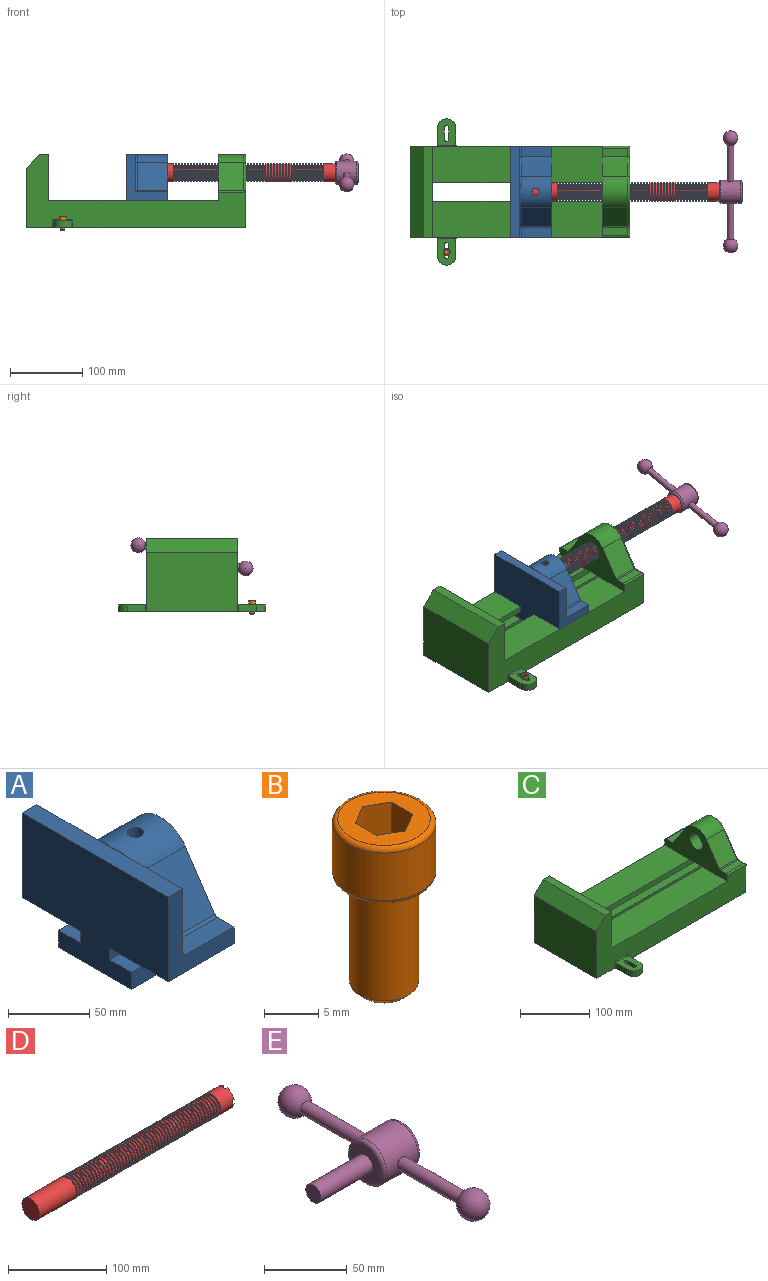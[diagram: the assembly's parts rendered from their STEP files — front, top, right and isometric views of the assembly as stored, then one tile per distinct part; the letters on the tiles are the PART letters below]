
ASSEMBLY  parts=5 mates=5
PART A: 36 faces, bbox 57.2x127x89 mm
  f0: plane 57.15x50.8mm, normal (0,0,-1), area 2903.2mm2, adj f6,f9,f10,f23
  f1: cylinder r=12.7mm len=44.45mm, axis (1,0,0), area 3464.3mm2, adj f6,f15,f16
  f2: plane 41.91x14.52mm, normal (0,0,1), area 608.5mm2, adj f6,f11,f24,f25
  f3: plane 51.86x48.26mm, normal (1,0,0), area 1495.7mm2, adj f8,f10,f31,f33,f35
  f4: plane 51.86x48.26mm, normal (1,0,0), area 1495.7mm2, adj f8,f11,f24,f28,f29
  f5: plane 57.15x50.8mm, normal (0,0,-1), area 2903.2mm2, adj f6,f9,f11,f22
  f6: plane 127x85.09mm, normal (1,0,0), area 5190.6mm2, adj f0,f1,f2,f5,f7,f10,f11,f12
  f7: plane 41.91x14.52mm, normal (0,0,1), area 608.5mm2, adj f6,f10,f30,f31
  f8: plane 127x12.7mm, normal (0,0,1), area 1612.9mm2, adj f3,f4,f9,f10,f11,f26,f34
  f9: plane 127x85.09mm, normal (-1,0,0), area 9096.8mm2, adj f0,f5,f8,f10,f11,f17,f18,f19
  f10: plane 63.5x57.15mm, normal (0,-1,0), area 1372.3mm2, adj f0,f3,f6,f7,f8,f9,f31
  f11: plane 63.5x57.15mm, normal (0,1,0), area 1372.3mm2, adj f2,f4,f5,f6,f8,f9,f24
  f12: plane 41.91x38.43mm, normal (0,-0.83,0.56), area 1939.2mm2, adj f6,f13,f30,f33
  f13: cylinder r=25.4mm len=44.45mm, axis (1,0,0), area 2026.5mm2, adj f6,f12,f14,f16,f26,f28,f34,f35
  f14: plane 41.91x38.43mm, normal (0,0.83,0.56), area 1939.2mm2, adj f6,f13,f25,f29
  f15: plane 25.4x25.4mm, normal (1,0,0), area 506.7mm2, adj f1
  f16: cylinder r=5.08mm len=13.76mm, axis (0,0,1), area 414mm2, adj f1,f13
  f17: plane 57.15x19.05mm, normal (0,0,1), area 1088.7mm2, adj f6,f9,f18,f23
  f18: plane 57.15x12.7mm, normal (0,-1,0), area 725.8mm2, adj f6,f9,f17,f19
  f19: plane 63.5x57.15mm, normal (0,0,-1), area 3629mm2, adj f6,f9,f18,f20
  f20: plane 57.15x12.7mm, normal (0,1,0), area 725.8mm2, adj f6,f9,f19,f21
  f21: plane 57.15x19.05mm, normal (0,0,1), area 1088.7mm2, adj f6,f9,f20,f22
  f22: plane 57.15x8.89mm, normal (0,1,0), area 508.1mm2, adj f5,f6,f9,f21
  f23: plane 57.15x8.89mm, normal (0,-1,0), area 508.1mm2, adj f0,f6,f9,f17
  f24: cylinder r=2.54mm len=14.52mm, axis (0,-1,0), area 57.9mm2, adj f2,f4,f11,f27
  f25: cylinder r=2.54mm len=41.91mm, axis (1,0,0), area 104.3mm2, adj f2,f6,f14,f27
  f26: bspline ~12.24x2.8mm, area 20.9mm2, adj f8,f13,f28
  f27: sphere r=2.54mm, area 6.3mm2, adj f24,f25,f29
  f28: torus R=27.94mm, axis (1,0,0), area 57.8mm2, adj f4,f13,f26,f29
  f29: cylinder r=2.54mm len=39.84mm, axis (0,-0.56,0.83), area 184.6mm2, adj f4,f14,f27,f28
  f30: cylinder r=2.54mm len=41.91mm, axis (1,0,0), area 104.3mm2, adj f6,f7,f12,f32
  f31: cylinder r=2.54mm len=14.52mm, axis (0,-1,0), area 57.9mm2, adj f3,f7,f10,f32
  f32: sphere r=2.54mm, area 6.3mm2, adj f30,f31,f33
  f33: cylinder r=2.54mm len=39.84mm, axis (0,-0.56,-0.83), area 184.6mm2, adj f3,f12,f32,f35
  f34: bspline ~12.24x2.8mm, area 20.9mm2, adj f8,f13,f35
  f35: torus R=27.94mm, axis (1,0,0), area 57.8mm2, adj f3,f13,f33,f34
PART B: 15 faces, bbox 10.3x10.3x19.1 mm
  f0: plane 8.51x8.51mm, normal (0,0,1), area 37.2mm2, adj f5,f6,f7,f8,f9,f10,f14
  f1: cylinder r=3.17mm len=11.94mm, axis (0,0,1), area 238.2mm2, adj f4,f12
  f2: plane 4.83x4.83mm, normal (0,0,-1), area 18.3mm2, adj f12
  f3: cylinder r=4.76mm len=9.53mm, axis (0,0,-1), area 159.6mm2, adj f13,f14
  f4: plane 8.51x8.51mm, normal (0,0,-1), area 25.2mm2, adj f1,f13
  f5: plane 4.83x2.38mm, normal (-0.5,-0.87,0), area 13.3mm2, adj f0,f6,f10,f11
  f6: plane 4.83x2.38mm, normal (0.5,-0.87,0), area 13.3mm2, adj f0,f5,f7,f11
  f7: plane 4.83x2.75mm, normal (1,0,0), area 13.3mm2, adj f0,f6,f8,f11
  f8: plane 4.83x2.38mm, normal (0.5,0.87,0), area 13.3mm2, adj f0,f7,f9,f11
  f9: plane 4.83x2.38mm, normal (-0.5,0.87,0), area 13.3mm2, adj f0,f8,f10,f11
  f10: plane 4.83x2.75mm, normal (-1,0,0), area 13.3mm2, adj f0,f5,f9,f11
  f11: plane 5.5x4.76mm, normal (0,0,1), area 19.6mm2, adj f5,f6,f7,f8,f9,f10
  f12: cone r=3.17mm half-angle=45deg, axis (0,0,1), area 18.9mm2, adj f1,f2
  f13: torus R=4.25mm, axis (0,0,1), area 23mm2, adj f3,f4
  f14: torus R=4.25mm, axis (0,0,1), area 23mm2, adj f0,f3
PART C: 61 faces, bbox 304.8x203.2x103.7 mm
  f0: plane 304.8x101.6mm, normal (0,1,0), area 13520.3mm2, adj f3,f4,f5,f6,f7,f8,f9,f16
  f1: plane 304.8x101.6mm, normal (0,-1,0), area 13520.3mm2, adj f2,f3,f5,f6,f7,f8,f9,f16
  f2: plane 234.95x50.8mm, normal (0,0,1), area 11935.5mm2, adj f1,f5,f16,f26
  f3: plane 127x99.06mm, normal (1,0,0), area 7097.5mm2, adj f0,f1,f9,f14,f17,f18,f19,f20
  f4: plane 234.95x50.8mm, normal (0,0,1), area 11935.5mm2, adj f0,f5,f16,f27
  f5: plane 127x101.6mm, normal (1,0,0), area 9516.1mm2, adj f0,f1,f2,f4,f6,f9,f18,f19
  f6: plane 127x12.7mm, normal (0,0,1), area 1612.9mm2, adj f0,f1,f5,f7
  f7: plane 127x19.05mm, normal (-0.71,0,0.71), area 3421.5mm2, adj f0,f1,f6,f8
  f8: plane 127x82.55mm, normal (-1,0,0), area 10483.8mm2, adj f0,f1,f7,f9
  f9: plane 304.8x203.2mm, normal (0,0,-1), area 33298.3mm2, adj f0,f1,f3,f5,f8,f21,f22,f39
  f10: plane 35.56x11.98mm, normal (0,0,1), area 426mm2, adj f16,f28,f29,f30
  f11: plane 38.43x35.56mm, normal (0,0.83,0.56), area 1645.4mm2, adj f12,f16,f29,f32
  f12: cylinder r=25.4mm len=42.19mm, axis (1,0,0), area 1770.2mm2, adj f11,f13,f16,f33
  f13: plane 38.43x35.56mm, normal (0,-0.83,0.56), area 1645.4mm2, adj f12,f16,f34,f35
  f14: cylinder r=12.7mm len=38.1mm, axis (1,0,0), area 3040.2mm2, adj f3,f16
  f15: plane 35.56x11.98mm, normal (0,0,1), area 426mm2, adj f16,f34,f36,f38
  f16: plane 127x63.5mm, normal (-1,0,0), area 4155.5mm2, adj f0,f1,f2,f4,f10,f11,f12,f13
  f17: plane 38.1x25.4mm, normal (0,0,-1), area 967.7mm2, adj f3,f16,f26,f27
  f18: plane 273.05x19.05mm, normal (0,0,-1), area 5201.6mm2, adj f3,f5,f19,f26
  f19: plane 273.05x12.7mm, normal (0,1,0), area 3467.7mm2, adj f3,f5,f18,f20
  f20: plane 273.05x19.05mm, normal (0,0,1), area 5201.6mm2, adj f3,f5,f19,f21
  f21: plane 273.05x16.51mm, normal (0,1,0), area 4508.1mm2, adj f3,f5,f9,f20
  f22: plane 273.05x16.51mm, normal (0,-1,0), area 4508.1mm2, adj f3,f5,f9,f23
  f23: plane 273.05x19.05mm, normal (0,0,1), area 5201.6mm2, adj f3,f5,f22,f24
  f24: plane 273.05x12.7mm, normal (0,-1,0), area 3467.7mm2, adj f3,f5,f23,f25
  f25: plane 273.05x19.05mm, normal (0,0,-1), area 5201.6mm2, adj f3,f5,f24,f27
  f26: plane 273.05x8.89mm, normal (0,1,0), area 2427.4mm2, adj f2,f3,f5,f17,f18
  f27: plane 273.05x8.89mm, normal (0,-1,0), area 2427.4mm2, adj f3,f4,f5,f17,f25
  f28: cylinder r=2.54mm len=38.1mm, axis (1,0,0), area 148.3mm2, adj f0,f10,f16,f30
  f29: cylinder r=2.54mm len=35.56mm, axis (-1,0,0), area 88.5mm2, adj f10,f11,f16,f31
  f30: cylinder r=2.54mm len=14.52mm, axis (0,1,0), area 54.3mm2, adj f3,f10,f28,f31
  f31: torus R=5.08mm, axis (-1,0,0), area 13.5mm2, adj f3,f29,f30,f32
  f32: cylinder r=2.54mm len=39.84mm, axis (0,0.56,-0.83), area 184.6mm2, adj f3,f11,f31,f33
  f33: torus R=22.86mm, axis (-1,0,0), area 191.4mm2, adj f3,f12,f32,f35
  f34: cylinder r=2.54mm len=35.56mm, axis (-1,0,0), area 88.5mm2, adj f13,f15,f16,f37
  f35: cylinder r=2.54mm len=39.84mm, axis (0,0.56,0.83), area 184.6mm2, adj f3,f13,f33,f37
  f36: cylinder r=2.54mm len=38.1mm, axis (-1,0,0), area 148.3mm2, adj f1,f15,f16,f38
  f37: torus R=5.08mm, axis (-1,0,0), area 13.5mm2, adj f3,f34,f35,f38
  f38: cylinder r=2.54mm len=14.52mm, axis (0,1,0), area 54.3mm2, adj f3,f15,f36,f37
  f39: plane 23.88x9.53mm, normal (-1,0,0), area 227.4mm2, adj f9,f45,f46,f60
  f40: plane 23.88x9.53mm, normal (1,0,0), area 227.4mm2, adj f9,f45,f46,f58
  f41: cylinder r=3.3mm len=9.53mm, axis (0,0,-1), area 98.8mm2, adj f9,f42,f44,f46
  f42: plane 15.62x9.53mm, normal (-1,0,0), area 148.8mm2, adj f9,f41,f43,f46
  f43: cylinder r=3.3mm len=9.53mm, axis (0,0,-1), area 98.8mm2, adj f9,f42,f44,f46
  f44: plane 15.62x9.53mm, normal (1,0,0), area 148.8mm2, adj f9,f41,f43,f46
  f45: cylinder r=12.7mm len=25.4mm, axis (0,0,-1), area 380mm2, adj f9,f39,f40,f46
  f46: plane 36.58x25.4mm, normal (0,0,1), area 722.4mm2, adj f39,f40,f41,f42,f43,f44,f45,f59
  f47: plane 23.88x9.53mm, normal (-1,0,0), area 227.4mm2, adj f9,f53,f54,f56
  f48: plane 23.88x9.53mm, normal (1,0,0), area 227.4mm2, adj f9,f53,f54,f55
  f49: cylinder r=3.3mm len=9.53mm, axis (0,0,-1), area 98.8mm2, adj f9,f50,f52,f54
  f50: plane 15.62x9.53mm, normal (-1,0,0), area 148.8mm2, adj f9,f49,f51,f54
  f51: cylinder r=3.3mm len=9.53mm, axis (0,0,-1), area 98.8mm2, adj f9,f50,f52,f54
  f52: plane 15.62x9.53mm, normal (1,0,0), area 148.8mm2, adj f9,f49,f51,f54
  f53: cylinder r=12.7mm len=25.4mm, axis (0,0,-1), area 380mm2, adj f9,f47,f48,f54
  f54: plane 36.58x25.4mm, normal (0,0,1), area 722.4mm2, adj f47,f48,f49,f50,f51,f52,f53,f57
  f55: cylinder r=1.52mm len=11.05mm, axis (0,0,-1), area 24.1mm2, adj f0,f9,f48,f57
  f56: cylinder r=1.52mm len=11.05mm, axis (0,0,1), area 24.1mm2, adj f0,f9,f47,f57
  f57: cylinder r=1.52mm len=28.45mm, axis (1,0,0), area 63.5mm2, adj f0,f54,f55,f56
  f58: cylinder r=1.52mm len=11.05mm, axis (0,0,1), area 24.1mm2, adj f1,f9,f40,f59
  f59: cylinder r=1.52mm len=28.45mm, axis (-1,0,0), area 63.5mm2, adj f1,f46,f58,f60
  f60: cylinder r=1.52mm len=11.05mm, axis (0,0,-1), area 24.1mm2, adj f1,f9,f39,f59
PART D: 220 faces, bbox 279.4x25.4x25.4 mm
  f0: cylinder r=12.7mm len=25.4mm, axis (-1,0,0), area 1468.2mm2, adj f1,f2,f3,f5,f7,f208,f209,f210
  f1: plane 9.9x9.9mm, normal (1,0,0), area 62.3mm2, adj f0,f4,f213,f216
  f2: plane 9.9x9.9mm, normal (1,0,0), area 62.3mm2, adj f0,f4,f210,f218
  f3: plane 9.9x9.9mm, normal (1,0,0), area 62.3mm2, adj f0,f4,f209,f212
  f4: cylinder r=6.35mm len=25.4mm, axis (1,0,0), area 960.3mm2, adj f1,f2,f3,f5,f6,f208,f209,f210
  f5: plane 9.9x9.9mm, normal (1,0,0), area 62.3mm2, adj f0,f4,f215,f217
  f6: plane 12.7x12.7mm, normal (1,0,0), area 126.7mm2, adj f4
  f7: cone r=12.7mm half-angle=76deg, axis (1,0,0), area 188mm2, adj f0,f9
  f8: cone r=10.16mm half-angle=76deg, axis (-1,0,0), area 188mm2, adj f9,f10
  f9: cylinder r=10.16mm len=20.32mm, axis (1,0,0), area 81.1mm2, adj f7,f8
  f10: cylinder r=12.7mm len=25.4mm, axis (-1,0,0), area 131.7mm2, adj f8,f11
  f11: cone r=12.7mm half-angle=76deg, axis (1,0,0), area 188mm2, adj f10,f13
  f12: cone r=10.16mm half-angle=76deg, axis (-1,0,0), area 188mm2, adj f13,f14
  f13: cylinder r=10.16mm len=20.32mm, axis (1,0,0), area 81.1mm2, adj f11,f12
  f14: cylinder r=12.7mm len=25.4mm, axis (-1,0,0), area 131.7mm2, adj f12,f15
  f15: cone r=12.7mm half-angle=76deg, axis (1,0,0), area 188mm2, adj f14,f17
  f16: cone r=10.16mm half-angle=76deg, axis (-1,0,0), area 188mm2, adj f17,f18
  f17: cylinder r=10.16mm len=20.32mm, axis (1,0,0), area 81.1mm2, adj f15,f16
  f18: cylinder r=12.7mm len=25.4mm, axis (-1,0,0), area 131.7mm2, adj f16,f19
  f19: cone r=12.7mm half-angle=76deg, axis (1,0,0), area 188mm2, adj f18,f21
  f20: cone r=10.16mm half-angle=76deg, axis (-1,0,0), area 188mm2, adj f21,f22
  f21: cylinder r=10.16mm len=20.32mm, axis (1,0,0), area 81.1mm2, adj f19,f20
  f22: cylinder r=12.7mm len=25.4mm, axis (-1,0,0), area 131.7mm2, adj f20,f23
  f23: cone r=12.7mm half-angle=76deg, axis (1,0,0), area 188mm2, adj f22,f25
  f24: cone r=10.16mm half-angle=76deg, axis (-1,0,0), area 188mm2, adj f25,f26
  f25: cylinder r=10.16mm len=20.32mm, axis (1,0,0), area 81.1mm2, adj f23,f24
  f26: cylinder r=12.7mm len=25.4mm, axis (-1,0,0), area 131.7mm2, adj f24,f27
  f27: cone r=12.7mm half-angle=76deg, axis (1,0,0), area 188mm2, adj f26,f29
  f28: cone r=10.16mm half-angle=76deg, axis (-1,0,0), area 188mm2, adj f29,f30
  f29: cylinder r=10.16mm len=20.32mm, axis (1,0,0), area 81.1mm2, adj f27,f28
  f30: cylinder r=12.7mm len=25.4mm, axis (-1,0,0), area 131.7mm2, adj f28,f31
  f31: cone r=12.7mm half-angle=76deg, axis (1,0,0), area 188mm2, adj f30,f33
  f32: cone r=10.16mm half-angle=76deg, axis (-1,0,0), area 188mm2, adj f33,f34
  f33: cylinder r=10.16mm len=20.32mm, axis (1,0,0), area 81.1mm2, adj f31,f32
  f34: cylinder r=12.7mm len=25.4mm, axis (-1,0,0), area 131.7mm2, adj f32,f35
  f35: cone r=12.7mm half-angle=76deg, axis (1,0,0), area 188mm2, adj f34,f37
  f36: cone r=10.16mm half-angle=76deg, axis (-1,0,0), area 188mm2, adj f37,f38
  f37: cylinder r=10.16mm len=20.32mm, axis (1,0,0), area 81.1mm2, adj f35,f36
  f38: cylinder r=12.7mm len=25.4mm, axis (-1,0,0), area 131.7mm2, adj f36,f39
  f39: cone r=12.7mm half-angle=76deg, axis (1,0,0), area 188mm2, adj f38,f41
  f40: cone r=10.16mm half-angle=76deg, axis (-1,0,0), area 188mm2, adj f41,f42
  f41: cylinder r=10.16mm len=20.32mm, axis (1,0,0), area 81.1mm2, adj f39,f40
  f42: cylinder r=12.7mm len=25.4mm, axis (-1,0,0), area 131.7mm2, adj f40,f43
  f43: cone r=12.7mm half-angle=76deg, axis (1,0,0), area 188mm2, adj f42,f45
  f44: cone r=10.16mm half-angle=76deg, axis (-1,0,0), area 188mm2, adj f45,f46
  f45: cylinder r=10.16mm len=20.32mm, axis (1,0,0), area 81.1mm2, adj f43,f44
  f46: cylinder r=12.7mm len=25.4mm, axis (-1,0,0), area 131.7mm2, adj f44,f47
  f47: cone r=12.7mm half-angle=76deg, axis (1,0,0), area 188mm2, adj f46,f49
  f48: cone r=10.16mm half-angle=76deg, axis (-1,0,0), area 188mm2, adj f49,f50
  f49: cylinder r=10.16mm len=20.32mm, axis (1,0,0), area 81.1mm2, adj f47,f48
  f50: cylinder r=12.7mm len=25.4mm, axis (-1,0,0), area 131.7mm2, adj f48,f51
  f51: cone r=12.7mm half-angle=76deg, axis (1,0,0), area 188mm2, adj f50,f53
  f52: cone r=10.16mm half-angle=76deg, axis (-1,0,0), area 188mm2, adj f53,f54
  f53: cylinder r=10.16mm len=20.32mm, axis (1,0,0), area 81.1mm2, adj f51,f52
  f54: cylinder r=12.7mm len=25.4mm, axis (-1,0,0), area 131.7mm2, adj f52,f55
  f55: cone r=12.7mm half-angle=76deg, axis (1,0,0), area 188mm2, adj f54,f57
  f56: cone r=10.16mm half-angle=76deg, axis (-1,0,0), area 188mm2, adj f57,f58
  f57: cylinder r=10.16mm len=20.32mm, axis (1,0,0), area 81.1mm2, adj f55,f56
  f58: cylinder r=12.7mm len=25.4mm, axis (-1,0,0), area 131.7mm2, adj f56,f59
  f59: cone r=12.7mm half-angle=76deg, axis (1,0,0), area 188mm2, adj f58,f61
  f60: cone r=10.16mm half-angle=76deg, axis (-1,0,0), area 188mm2, adj f61,f62
  f61: cylinder r=10.16mm len=20.32mm, axis (1,0,0), area 81.1mm2, adj f59,f60
  f62: cylinder r=12.7mm len=25.4mm, axis (-1,0,0), area 131.7mm2, adj f60,f63
  f63: cone r=12.7mm half-angle=76deg, axis (1,0,0), area 188mm2, adj f62,f65
  f64: cone r=10.16mm half-angle=76deg, axis (-1,0,0), area 188mm2, adj f65,f66
  f65: cylinder r=10.16mm len=20.32mm, axis (1,0,0), area 81.1mm2, adj f63,f64
  f66: cylinder r=12.7mm len=25.4mm, axis (-1,0,0), area 131.7mm2, adj f64,f67
  f67: cone r=12.7mm half-angle=76deg, axis (1,0,0), area 188mm2, adj f66,f69
  f68: cone r=10.16mm half-angle=76deg, axis (-1,0,0), area 188mm2, adj f69,f70
  f69: cylinder r=10.16mm len=20.32mm, axis (1,0,0), area 81.1mm2, adj f67,f68
  f70: cylinder r=12.7mm len=25.4mm, axis (-1,0,0), area 131.7mm2, adj f68,f71
  f71: cone r=12.7mm half-angle=76deg, axis (1,0,0), area 188mm2, adj f70,f73
  f72: cone r=10.16mm half-angle=76deg, axis (-1,0,0), area 188mm2, adj f73,f74
  f73: cylinder r=10.16mm len=20.32mm, axis (1,0,0), area 81.1mm2, adj f71,f72
  f74: cylinder r=12.7mm len=25.4mm, axis (-1,0,0), area 131.7mm2, adj f72,f75
  f75: cone r=12.7mm half-angle=76deg, axis (1,0,0), area 188mm2, adj f74,f77
  f76: cone r=10.16mm half-angle=76deg, axis (-1,0,0), area 188mm2, adj f77,f78
  f77: cylinder r=10.16mm len=20.32mm, axis (1,0,0), area 81.1mm2, adj f75,f76
  f78: cylinder r=12.7mm len=25.4mm, axis (-1,0,0), area 131.7mm2, adj f76,f79
  f79: cone r=12.7mm half-angle=76deg, axis (1,0,0), area 188mm2, adj f78,f81
  f80: cone r=10.16mm half-angle=76deg, axis (-1,0,0), area 188mm2, adj f81,f82
  f81: cylinder r=10.16mm len=20.32mm, axis (1,0,0), area 81.1mm2, adj f79,f80
  f82: cylinder r=12.7mm len=25.4mm, axis (-1,0,0), area 131.7mm2, adj f80,f83
  f83: cone r=12.7mm half-angle=76deg, axis (1,0,0), area 188mm2, adj f82,f85
  f84: cone r=10.16mm half-angle=76deg, axis (-1,0,0), area 188mm2, adj f85,f86
  f85: cylinder r=10.16mm len=20.32mm, axis (1,0,0), area 81.1mm2, adj f83,f84
  f86: cylinder r=12.7mm len=25.4mm, axis (-1,0,0), area 131.7mm2, adj f84,f87
  f87: cone r=12.7mm half-angle=76deg, axis (1,0,0), area 188mm2, adj f86,f89
  f88: cone r=10.16mm half-angle=76deg, axis (-1,0,0), area 188mm2, adj f89,f90
  f89: cylinder r=10.16mm len=20.32mm, axis (1,0,0), area 81.1mm2, adj f87,f88
  f90: cylinder r=12.7mm len=25.4mm, axis (-1,0,0), area 131.7mm2, adj f88,f91
  f91: cone r=12.7mm half-angle=76deg, axis (1,0,0), area 188mm2, adj f90,f93
  f92: cone r=10.16mm half-angle=76deg, axis (-1,0,0), area 188mm2, adj f93,f94
  f93: cylinder r=10.16mm len=20.32mm, axis (1,0,0), area 81.1mm2, adj f91,f92
  f94: cylinder r=12.7mm len=25.4mm, axis (-1,0,0), area 131.7mm2, adj f92,f95
  f95: cone r=12.7mm half-angle=76deg, axis (1,0,0), area 188mm2, adj f94,f97
  f96: cone r=10.16mm half-angle=76deg, axis (-1,0,0), area 188mm2, adj f97,f98
  f97: cylinder r=10.16mm len=20.32mm, axis (1,0,0), area 81.1mm2, adj f95,f96
  f98: cylinder r=12.7mm len=25.4mm, axis (-1,0,0), area 131.7mm2, adj f96,f99
  f99: cone r=12.7mm half-angle=76deg, axis (1,0,0), area 188mm2, adj f98,f101
  f100: cone r=10.16mm half-angle=76deg, axis (-1,0,0), area 188mm2, adj f101,f102
  f101: cylinder r=10.16mm len=20.32mm, axis (1,0,0), area 81.1mm2, adj f99,f100
  f102: cylinder r=12.7mm len=25.4mm, axis (-1,0,0), area 131.7mm2, adj f100,f103
  f103: cone r=12.7mm half-angle=76deg, axis (1,0,0), area 188mm2, adj f102,f105
  f104: cone r=10.16mm half-angle=76deg, axis (-1,0,0), area 188mm2, adj f105,f106
  f105: cylinder r=10.16mm len=20.32mm, axis (1,0,0), area 81.1mm2, adj f103,f104
  f106: cylinder r=12.7mm len=25.4mm, axis (-1,0,0), area 131.7mm2, adj f104,f107
  f107: cone r=12.7mm half-angle=76deg, axis (1,0,0), area 188mm2, adj f106,f109
  f108: cone r=10.16mm half-angle=76deg, axis (-1,0,0), area 188mm2, adj f109,f110
  f109: cylinder r=10.16mm len=20.32mm, axis (1,0,0), area 81.1mm2, adj f107,f108
  f110: cylinder r=12.7mm len=25.4mm, axis (-1,0,0), area 131.7mm2, adj f108,f111
  f111: cone r=12.7mm half-angle=76deg, axis (1,0,0), area 188mm2, adj f110,f113
  f112: cone r=10.16mm half-angle=76deg, axis (-1,0,0), area 188mm2, adj f113,f114
  f113: cylinder r=10.16mm len=20.32mm, axis (1,0,0), area 81.1mm2, adj f111,f112
  f114: cylinder r=12.7mm len=25.4mm, axis (-1,0,0), area 131.7mm2, adj f112,f115
  f115: cone r=12.7mm half-angle=76deg, axis (1,0,0), area 188mm2, adj f114,f117
  f116: cone r=10.16mm half-angle=76deg, axis (-1,0,0), area 188mm2, adj f117,f118
  f117: cylinder r=10.16mm len=20.32mm, axis (1,0,0), area 81.1mm2, adj f115,f116
  f118: cylinder r=12.7mm len=25.4mm, axis (-1,0,0), area 131.7mm2, adj f116,f119
  f119: cone r=12.7mm half-angle=76deg, axis (1,0,0), area 188mm2, adj f118,f121
  f120: cone r=10.16mm half-angle=76deg, axis (-1,0,0), area 188mm2, adj f121,f122
  f121: cylinder r=10.16mm len=20.32mm, axis (1,0,0), area 81.1mm2, adj f119,f120
  f122: cylinder r=12.7mm len=25.4mm, axis (-1,0,0), area 131.7mm2, adj f120,f123
  f123: cone r=12.7mm half-angle=76deg, axis (1,0,0), area 188mm2, adj f122,f125
  f124: cone r=10.16mm half-angle=76deg, axis (-1,0,0), area 188mm2, adj f125,f126
  f125: cylinder r=10.16mm len=20.32mm, axis (1,0,0), area 81.1mm2, adj f123,f124
  f126: cylinder r=12.7mm len=25.4mm, axis (-1,0,0), area 131.7mm2, adj f124,f127
  f127: cone r=12.7mm half-angle=76deg, axis (1,0,0), area 188mm2, adj f126,f129
  f128: cone r=10.16mm half-angle=76deg, axis (-1,0,0), area 188mm2, adj f129,f130
  f129: cylinder r=10.16mm len=20.32mm, axis (1,0,0), area 81.1mm2, adj f127,f128
  f130: cylinder r=12.7mm len=25.4mm, axis (-1,0,0), area 131.7mm2, adj f128,f131
  f131: cone r=12.7mm half-angle=76deg, axis (1,0,0), area 188mm2, adj f130,f133
  f132: cone r=10.16mm half-angle=76deg, axis (-1,0,0), area 188mm2, adj f133,f134
  f133: cylinder r=10.16mm len=20.32mm, axis (1,0,0), area 81.1mm2, adj f131,f132
  f134: cylinder r=12.7mm len=25.4mm, axis (-1,0,0), area 131.7mm2, adj f132,f135
  f135: cone r=12.7mm half-angle=76deg, axis (1,0,0), area 188mm2, adj f134,f137
  f136: cone r=10.16mm half-angle=76deg, axis (-1,0,0), area 188mm2, adj f137,f138
  f137: cylinder r=10.16mm len=20.32mm, axis (1,0,0), area 81.1mm2, adj f135,f136
  f138: cylinder r=12.7mm len=25.4mm, axis (-1,0,0), area 131.7mm2, adj f136,f139
  f139: cone r=12.7mm half-angle=76deg, axis (1,0,0), area 188mm2, adj f138,f141
  f140: cone r=10.16mm half-angle=76deg, axis (-1,0,0), area 188mm2, adj f141,f142
  f141: cylinder r=10.16mm len=20.32mm, axis (1,0,0), area 81.1mm2, adj f139,f140
  f142: cylinder r=12.7mm len=25.4mm, axis (-1,0,0), area 131.7mm2, adj f140,f143
  f143: cone r=12.7mm half-angle=76deg, axis (1,0,0), area 188mm2, adj f142,f145
  f144: cone r=10.16mm half-angle=76deg, axis (-1,0,0), area 188mm2, adj f145,f146
  f145: cylinder r=10.16mm len=20.32mm, axis (1,0,0), area 81.1mm2, adj f143,f144
  f146: cylinder r=12.7mm len=25.4mm, axis (-1,0,0), area 131.7mm2, adj f144,f147
  f147: cone r=12.7mm half-angle=76deg, axis (1,0,0), area 188mm2, adj f146,f149
  f148: cone r=10.16mm half-angle=76deg, axis (-1,0,0), area 188mm2, adj f149,f150
  f149: cylinder r=10.16mm len=20.32mm, axis (1,0,0), area 81.1mm2, adj f147,f148
  f150: cylinder r=12.7mm len=25.4mm, axis (-1,0,0), area 131.7mm2, adj f148,f151
  f151: cone r=12.7mm half-angle=76deg, axis (1,0,0), area 188mm2, adj f150,f153
  f152: cone r=10.16mm half-angle=76deg, axis (-1,0,0), area 188mm2, adj f153,f154
  f153: cylinder r=10.16mm len=20.32mm, axis (1,0,0), area 81.1mm2, adj f151,f152
  f154: cylinder r=12.7mm len=25.4mm, axis (-1,0,0), area 131.7mm2, adj f152,f155
  f155: cone r=12.7mm half-angle=76deg, axis (1,0,0), area 188mm2, adj f154,f157
  f156: cone r=10.16mm half-angle=76deg, axis (-1,0,0), area 188mm2, adj f157,f158
  f157: cylinder r=10.16mm len=20.32mm, axis (1,0,0), area 81.1mm2, adj f155,f156
  f158: cylinder r=12.7mm len=25.4mm, axis (-1,0,0), area 131.7mm2, adj f156,f159
  f159: cone r=12.7mm half-angle=76deg, axis (1,0,0), area 188mm2, adj f158,f161
  f160: cone r=10.16mm half-angle=76deg, axis (-1,0,0), area 188mm2, adj f161,f162
  f161: cylinder r=10.16mm len=20.32mm, axis (1,0,0), area 81.1mm2, adj f159,f160
  f162: cylinder r=12.7mm len=25.4mm, axis (-1,0,0), area 131.7mm2, adj f160,f163
  f163: cone r=12.7mm half-angle=76deg, axis (1,0,0), area 188mm2, adj f162,f165
  f164: cone r=10.16mm half-angle=76deg, axis (-1,0,0), area 188mm2, adj f165,f166
  f165: cylinder r=10.16mm len=20.32mm, axis (1,0,0), area 81.1mm2, adj f163,f164
  f166: cylinder r=12.7mm len=25.4mm, axis (-1,0,0), area 131.7mm2, adj f164,f167
  f167: cone r=12.7mm half-angle=76deg, axis (1,0,0), area 188mm2, adj f166,f169
  f168: cone r=10.16mm half-angle=76deg, axis (-1,0,0), area 188mm2, adj f169,f170
  f169: cylinder r=10.16mm len=20.32mm, axis (1,0,0), area 81.1mm2, adj f167,f168
  f170: cylinder r=12.7mm len=25.4mm, axis (-1,0,0), area 131.7mm2, adj f168,f171
  f171: cone r=12.7mm half-angle=76deg, axis (1,0,0), area 188mm2, adj f170,f173
  f172: cone r=10.16mm half-angle=76deg, axis (-1,0,0), area 188mm2, adj f173,f174
  f173: cylinder r=10.16mm len=20.32mm, axis (1,0,0), area 81.1mm2, adj f171,f172
  f174: cylinder r=12.7mm len=25.4mm, axis (-1,0,0), area 131.7mm2, adj f172,f175
  f175: cone r=12.7mm half-angle=76deg, axis (1,0,0), area 188mm2, adj f174,f177
  f176: cone r=10.16mm half-angle=76deg, axis (-1,0,0), area 188mm2, adj f177,f178
  f177: cylinder r=10.16mm len=20.32mm, axis (1,0,0), area 81.1mm2, adj f175,f176
  f178: cylinder r=12.7mm len=25.4mm, axis (-1,0,0), area 131.7mm2, adj f176,f179
  f179: cone r=12.7mm half-angle=76deg, axis (1,0,0), area 188mm2, adj f178,f181
  f180: cone r=10.16mm half-angle=76deg, axis (-1,0,0), area 188mm2, adj f181,f182
  f181: cylinder r=10.16mm len=20.32mm, axis (1,0,0), area 81.1mm2, adj f179,f180
  f182: cylinder r=12.7mm len=25.4mm, axis (-1,0,0), area 131.7mm2, adj f180,f183
  f183: cone r=12.7mm half-angle=76deg, axis (1,0,0), area 188mm2, adj f182,f185
  f184: cone r=10.16mm half-angle=76deg, axis (-1,0,0), area 188mm2, adj f185,f186
  f185: cylinder r=10.16mm len=20.32mm, axis (1,0,0), area 81.1mm2, adj f183,f184
  f186: cylinder r=12.7mm len=25.4mm, axis (-1,0,0), area 131.7mm2, adj f184,f187
  f187: cone r=12.7mm half-angle=76deg, axis (1,0,0), area 188mm2, adj f186,f189
  f188: cone r=10.16mm half-angle=76deg, axis (-1,0,0), area 188mm2, adj f189,f190
  f189: cylinder r=10.16mm len=20.32mm, axis (1,0,0), area 81.1mm2, adj f187,f188
  f190: cylinder r=12.7mm len=25.4mm, axis (-1,0,0), area 131.7mm2, adj f188,f191
  f191: cone r=12.7mm half-angle=76deg, axis (1,0,0), area 188mm2, adj f190,f193
  f192: cone r=10.16mm half-angle=76deg, axis (-1,0,0), area 188mm2, adj f193,f194
  f193: cylinder r=10.16mm len=20.32mm, axis (1,0,0), area 81.1mm2, adj f191,f192
  f194: cylinder r=12.7mm len=25.4mm, axis (-1,0,0), area 131.7mm2, adj f192,f195
  f195: cone r=12.7mm half-angle=76deg, axis (1,0,0), area 188mm2, adj f194,f197
  f196: cone r=10.16mm half-angle=76deg, axis (-1,0,0), area 188mm2, adj f197,f198
  f197: cylinder r=10.16mm len=20.32mm, axis (1,0,0), area 81.1mm2, adj f195,f196
  f198: cylinder r=12.7mm len=25.4mm, axis (-1,0,0), area 131.7mm2, adj f196,f199
  f199: cone r=12.7mm half-angle=76deg, axis (1,0,0), area 188mm2, adj f198,f201
  f200: cone r=10.16mm half-angle=76deg, axis (-1,0,0), area 188mm2, adj f201,f202
  f201: cylinder r=10.16mm len=20.32mm, axis (1,0,0), area 81.1mm2, adj f199,f200
  f202: cylinder r=12.7mm len=25.4mm, axis (-1,0,0), area 131.7mm2, adj f200,f203
  f203: cone r=12.7mm half-angle=76deg, axis (1,0,0), area 188mm2, adj f202,f205
  f204: cone r=10.16mm half-angle=76deg, axis (-1,0,0), area 188mm2, adj f205,f207
  f205: cylinder r=10.16mm len=20.32mm, axis (1,0,0), area 81.1mm2, adj f203,f204
  f206: plane 25.4x25.4mm, normal (-1,0,0), area 506.7mm2, adj f207
  f207: cylinder r=12.7mm len=52.45mm, axis (-1,0,0), area 4185.4mm2, adj f204,f206
  f208: plane 6.88x5.08mm, normal (1,0,0), area 32.7mm2, adj f0,f4,f209,f210
  f209: plane 6.62x2.54mm, normal (0,-1,0), area 16.8mm2, adj f0,f3,f4,f208
  f210: plane 6.62x2.54mm, normal (0,1,0), area 16.8mm2, adj f0,f2,f4,f208
  f211: plane 6.88x5.08mm, normal (1,0,0), area 32.7mm2, adj f0,f4,f212,f213
  f212: plane 6.62x2.54mm, normal (0,0,1), area 16.8mm2, adj f0,f3,f4,f211
  f213: plane 6.62x2.54mm, normal (0,0,-1), area 16.8mm2, adj f0,f1,f4,f211
  f214: plane 6.88x5.08mm, normal (1,0,0), area 32.7mm2, adj f0,f4,f215,f216
  f215: plane 6.62x2.54mm, normal (0,1,0), area 16.8mm2, adj f0,f4,f5,f214
  f216: plane 6.62x2.54mm, normal (0,-1,0), area 16.8mm2, adj f0,f1,f4,f214
  f217: plane 6.62x2.54mm, normal (0,0,-1), area 16.8mm2, adj f0,f4,f5,f219
  f218: plane 6.62x2.54mm, normal (0,0,1), area 16.8mm2, adj f0,f2,f4,f219
  f219: plane 6.88x5.08mm, normal (1,0,0), area 32.7mm2, adj f0,f4,f217,f218
PART E: 11 faces, bbox 76.2x172.7x34.4 mm
  f0: sphere r=10.16mm, area 1231.8mm2, adj f1
  f1: cylinder r=4.45mm len=51.82mm, axis (0,1,0), area 1438.5mm2, adj f0,f4
  f2: sphere r=10.16mm, area 1231.8mm2, adj f3
  f3: cylinder r=4.45mm len=51.82mm, axis (0,1,0), area 1438.5mm2, adj f2,f4
  f4: cylinder r=15.88mm len=31.75mm, axis (-1,0,0), area 2534.7mm2, adj f1,f3,f9,f10
  f5: cylinder r=6.35mm len=44.45mm, axis (-1,0,0), area 1773.5mm2, adj f6,f8
  f6: plane 12.7x12.7mm, normal (-1,0,0), area 126.7mm2, adj f5
  f7: plane 26.67x26.67mm, normal (1,0,0), area 558.6mm2, adj f10
  f8: plane 26.67x26.67mm, normal (-1,0,0), area 432mm2, adj f5,f9
  f9: torus R=13.33mm, axis (1,0,0), area 374.8mm2, adj f4,f8
  f10: torus R=13.33mm, axis (1,0,0), area 374.8mm2, adj f4,f7
PLACE A t=(107.52,0,0)mm
PLACE B rot(axis=(0,0,1),153.6deg) t=(-254,-83.45,9.52)mm
PLACE C at identity fixed
PLACE D rot(axis=(1,0,0),12.2deg) t=(107.52,16.08,1.72)mm
PLACE E rot(axis=(1,0,0),12.2deg) t=(85.93,16.08,1.72)mm
MATE fastened D.f4 <-> E.f5  axis (1,0,0) through (124.03,0,76.2)mm
MATE planar A.f0 <-> C.f2  axis (0,0,-1) through (-136.95,-38.1,38.1)mm
MATE pin_slot B.f1 <-> C.f41  axis (0,0,1) through (-254,-83.45,9.52)mm
MATE revolute D.f7 <-> A.f28  axis (-1,0,0) through (-152.83,0,76.2)mm
MATE cylindrical C.f12 <-> D.f7  axis (-1,0,0) through (-38.1,0,76.2)mm
